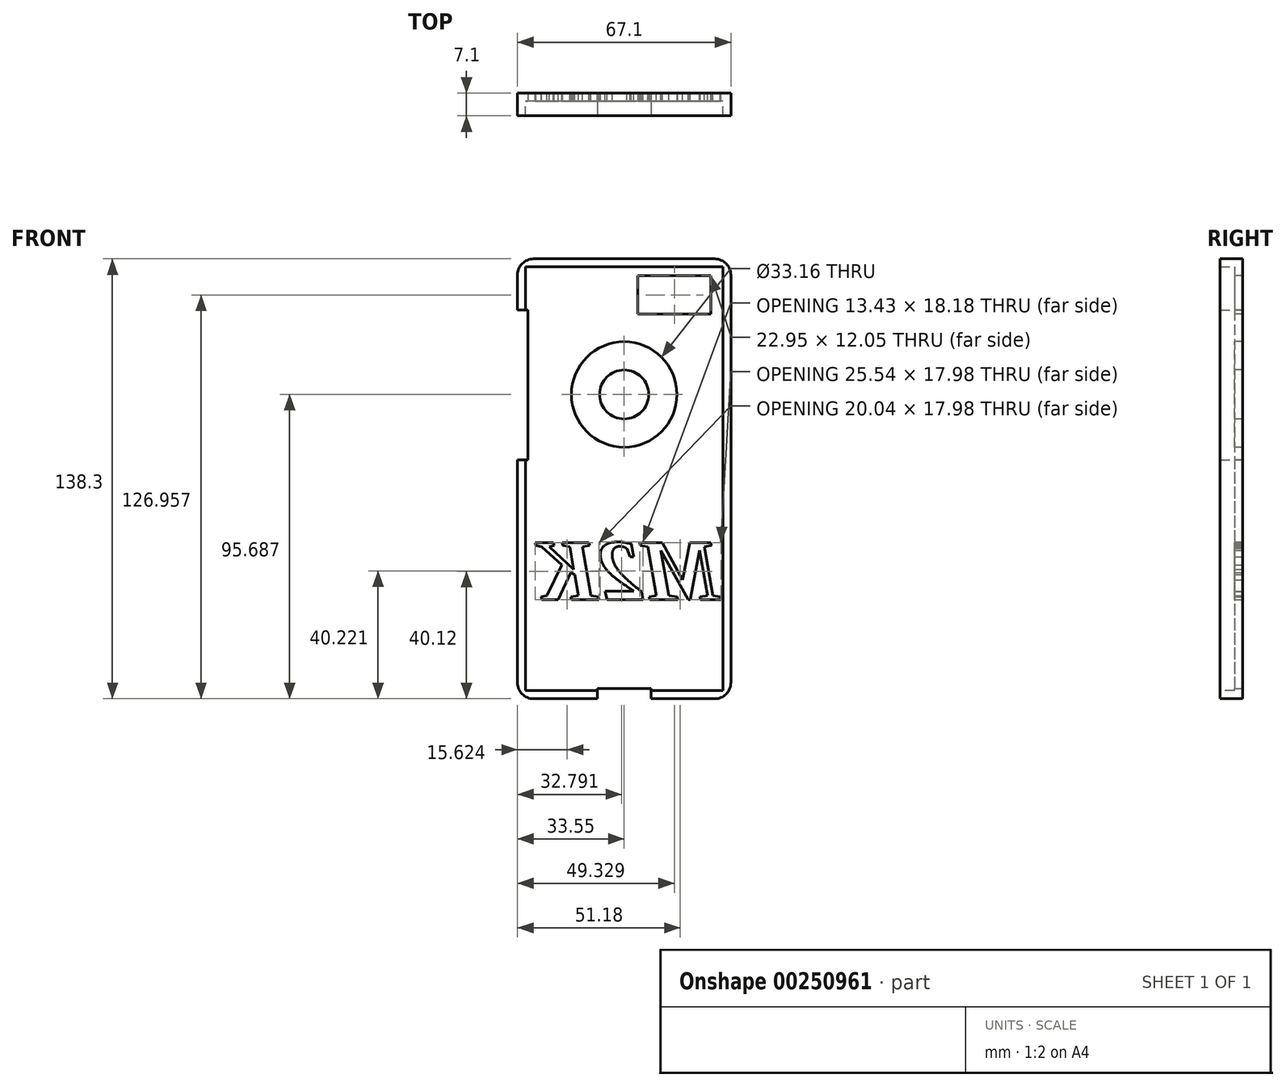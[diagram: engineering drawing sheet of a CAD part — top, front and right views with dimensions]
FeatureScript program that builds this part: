
annotation { "Feature Type Name" : "Feature", "Feature Type Description" : "" }
export const myFeature = defineFeature(function(context is Context, id is Id, definition is map)
    precondition{}
    {
        {
            var Q0;
            Q0=qCreatedBy(makeId("Front.planeOp"),FACE);
            var sketch = newSketch(context, id + "F0", { "sketchPlane" : qUnion([Q0])});
            skLineSegment(sketch, "E0.bottom", {"start": v(33.55, 69.15) * mm, "end": v(-33.55, 69.15) * mm});
            skLineSegment(sketch, "E0.top", {"start": v(33.55, -69.15) * mm, "end": v(-33.55, -69.15) * mm});
            skLineSegment(sketch, "E0.left", {"start": v(33.55, 69.15) * mm, "end": v(33.55, -69.15) * mm});
            skLineSegment(sketch, "E0.right", {"start": v(-33.55, 69.15) * mm, "end": v(-33.55, -69.15) * mm});
            skPoint(sketch, "E0.middle", {"position": v(0, 0) * mm});
            skSolve(sketch);
        }
        {
            var Q0;
            Q0=makeQuery(id+"F0.imprint","IMPRINT",FACE,{"disambiguationData":[TD([[makeQuery(id+"F0.imprint","IMPRINT",EDGE,{"derivedFrom":sQuery(id+"F0.wireOp",EDGE,"E0.bottom")}),1.0]])]});
            extrude(context, id + "F1", {"entities" : qUnion([Q0]), "endBound" : BoundingType.SYMMETRIC, "depth" : 7.1 * mm});
        }
        {
            var Q0;
            Q0=makeQuery(id+"F1.opExtrude","CAP_FACE",FACE,{"disambiguationData":[OSD([sQuery(id+"F0.wireOp",EDGE,"E0.bottom"),sQuery(id+"F0.wireOp",EDGE,"E0.top"),sQuery(id+"F0.wireOp",EDGE,"E0.left"),sQuery(id+"F0.wireOp",EDGE,"E0.right")])],"isStart":false});
            shell(context, id + "F2", {"entities" : qUnion([Q0]), "thickness" : 2.54 * mm});
        }
        {
            var Q0;
            Q0=makeQuery(id+"F1.opExtrude","SWEPT_EDGE",EDGE,{"disambiguationData":[OSD([sQuery(id+"F0.wireOp",EDGE,"E0.bottom"),sQuery(id+"F0.wireOp",EDGE,"E0.left")])]});
            var Q1;
            Q1=makeQuery(id+"F1.opExtrude","SWEPT_EDGE",EDGE,{"disambiguationData":[OSD([sQuery(id+"F0.wireOp",EDGE,"E0.top"),sQuery(id+"F0.wireOp",EDGE,"E0.left")])]});
            var Q2;
            Q2=makeQuery(id+"F1.opExtrude","SWEPT_EDGE",EDGE,{"disambiguationData":[OSD([sQuery(id+"F0.wireOp",EDGE,"E0.top"),sQuery(id+"F0.wireOp",EDGE,"E0.right")])]});
            var Q3;
            Q3=makeQuery(id+"F1.opExtrude","SWEPT_EDGE",EDGE,{"disambiguationData":[OSD([sQuery(id+"F0.wireOp",EDGE,"E0.bottom"),sQuery(id+"F0.wireOp",EDGE,"E0.right")])]});
            fillet(context, id + "F3", {"entities" : qUnion([Q0, Q1, Q2, Q3]), "radius" : 5.08 * mm, "tangentPropagation" : true, "allowEdgeOverflow" : false});
        }
        {
            var Q0;
            Q0=makeQuery(id+"F2.opShell","OFFSET_FACE",FACE,{"disambiguationData":[OSD([sQuery(id+"F0.wireOp",EDGE,"E0.bottom"),sQuery(id+"F0.wireOp",EDGE,"E0.top"),sQuery(id+"F0.wireOp",EDGE,"E0.left"),sQuery(id+"F0.wireOp",EDGE,"E0.right")])]});
            var sketch = newSketch(context, id + "F4", { "sketchPlane" : qUnion([Q0])});
            skLineSegment(sketch, "E1.bottom", {"start": v(4.3, 63.83) * mm, "end": v(27.25, 63.83) * mm});
            skLineSegment(sketch, "E1.top", {"start": v(4.3, 51.78) * mm, "end": v(27.25, 51.78) * mm});
            skLineSegment(sketch, "E1.left", {"start": v(4.3, 63.83) * mm, "end": v(4.3, 51.78) * mm});
            skLineSegment(sketch, "E1.right", {"start": v(27.25, 63.83) * mm, "end": v(27.25, 51.78) * mm});
            skSolve(sketch);
        }
        {
            var Q0;
            Q0=makeQuery(id+"F4.imprint","IMPRINT",FACE,{"disambiguationData":[TD([[makeQuery(id+"F4.imprint","IMPRINT",EDGE,{"derivedFrom":sQuery(id+"F4.wireOp",EDGE,"E1.bottom")}),-1.0]])]});
            extrude(context, id + "F5", {"entities" : qUnion([Q0]), "operationType" : NewBodyOperationType.REMOVE, "endBound" : BoundingType.SYMMETRIC, "oppositeDirection" : true, "depth" : 25 * mm});
        }
        {
            var Q0;
            Q0=makeQuery(id+"F1.opExtrude","SWEPT_FACE",FACE,{"disambiguationData":[OSD([sQuery(id+"F0.wireOp",EDGE,"E0.top")])]});
            var sketch = newSketch(context, id + "F6", { "sketchPlane" : qUnion([Q0])});
            skLineSegment(sketch, "E2.bottom", {"start": v(8.47, 3.55) * mm, "end": v(-8.47, 3.55) * mm});
            skLineSegment(sketch, "E2.top", {"start": v(8.47, -3.55) * mm, "end": v(-8.47, -3.55) * mm});
            skLineSegment(sketch, "E2.left", {"start": v(8.47, 3.55) * mm, "end": v(8.47, -3.55) * mm});
            skLineSegment(sketch, "E2.right", {"start": v(-8.47, 3.55) * mm, "end": v(-8.47, -3.55) * mm});
            skPoint(sketch, "E2.middle", {"position": v(0, 0) * mm});
            skSolve(sketch);
        }
        {
            var Q0;
            Q0=makeQuery(id+"F6.imprint","IMPRINT",FACE,{"disambiguationData":[TD([[makeQuery(id+"F6.imprint","IMPRINT",EDGE,{"derivedFrom":sQuery(id+"F6.wireOp",EDGE,"E2.bottom")}),1.0]])]});
            extrude(context, id + "F7", {"entities" : qUnion([Q0]), "operationType" : NewBodyOperationType.REMOVE, "endBound" : BoundingType.SYMMETRIC, "depth" : 6.5 * mm});
        }
        {
            var Q0;
            Q0=makeQuery(id+"F1.opExtrude","SWEPT_FACE",FACE,{"disambiguationData":[OSD([sQuery(id+"F0.wireOp",EDGE,"E0.right")])]});
            var sketch = newSketch(context, id + "F8", { "sketchPlane" : qUnion([Q0])});
            skLineSegment(sketch, "E3.bottom", {"start": v(-3.55, 6.02) * mm, "end": v(3.55, 6.02) * mm});
            skLineSegment(sketch, "E3.top", {"start": v(-3.55, 53.07) * mm, "end": v(3.55, 53.07) * mm});
            skLineSegment(sketch, "E3.left", {"start": v(-3.55, 6.02) * mm, "end": v(-3.55, 53.07) * mm});
            skLineSegment(sketch, "E3.right", {"start": v(3.55, 6.02) * mm, "end": v(3.55, 53.07) * mm});
            skSolve(sketch);
        }
        {
            var Q0;
            Q0=makeQuery(id+"F8.imprint","IMPRINT",FACE,{"disambiguationData":[TD([[makeQuery(id+"F8.imprint","IMPRINT",EDGE,{"derivedFrom":sQuery(id+"F8.wireOp",EDGE,"E3.bottom")}),1.0]])]});
            extrude(context, id + "F9", {"entities" : qUnion([Q0]), "operationType" : NewBodyOperationType.REMOVE, "endBound" : BoundingType.SYMMETRIC, "oppositeDirection" : true, "depth" : 6.5 * mm});
        }
        {
            var Q0;
            Q0=makeQuery(id+"F2.opShell","OFFSET_FACE",FACE,{"disambiguationData":[OSD([sQuery(id+"F0.wireOp",EDGE,"E0.bottom"),sQuery(id+"F0.wireOp",EDGE,"E0.top"),sQuery(id+"F0.wireOp",EDGE,"E0.left"),sQuery(id+"F0.wireOp",EDGE,"E0.right")])]});
            var sketch = newSketch(context, id + "F10", { "sketchPlane" : qUnion([Q0])});
            skCircle(sketch, "E4", {"center": v(0, 26.54) * mm, "radius": 16.58 * mm});
            skCircle(sketch, "E5", {"center": v(0, 26.54) * mm, "radius": 7.7 * mm});
            skSolve(sketch);
        }
        {
            var Q0;
            Q0 = qSketchRegion(id + "F10", true);
            extrude(context, id + "F11", {"entities" : qUnion([Q0]), "operationType" : NewBodyOperationType.REMOVE, "endBound" : BoundingType.SYMMETRIC, "oppositeDirection" : true, "depth" : 25 * mm});
        }
        {
            var Q0;
            {var subQ0=sQuery(id+"F0.wireOp",EDGE,"E0.top");var subQ1=sQuery(id+"F0.wireOp",EDGE,"E0.right");var subQ2=sQuery(id+"F0.wireOp",EDGE,"E0.bottom");var subQ3=sQuery(id+"F0.wireOp",EDGE,"E0.left");Q0=makeQuery(id+"F11.boolean.opBoolean","SPLIT",FACE,{"disambiguationData":[TD([makeQuery(id+"F1.opExtrude","SWEPT_FACE",FACE,{"disambiguationData":[OSD([subQ2])]})])],"derivedFrom":makeQuery(id+"F1.opExtrude","CAP_FACE",FACE,{"disambiguationData":[OSD([subQ2,subQ0,subQ3,subQ1])],"isStart":true})});}
            var sketch = newSketch(context, id + "F12", { "sketchPlane" : qUnion([Q0])});
            skText(sketch, "E6", { "text": "M2K", "fontName": "Tinos-BoldItalic.ttf"});
            const initialGuessF12  = {"E6": [-0.03004, -0.03802, 1, 0, 0.01977]};
            skSetInitialGuess(sketch, initialGuessF12);
            skSolve(sketch);
        }
        {
            var Q0;
            Q0 = qSketchRegion(id + "F12", true);
            extrude(context, id + "F13", {"entities" : qUnion([Q0]), "operationType" : NewBodyOperationType.REMOVE, "endBound" : BoundingType.SYMMETRIC, "oppositeDirection" : true, "depth" : 25 * mm});
        }
    });
